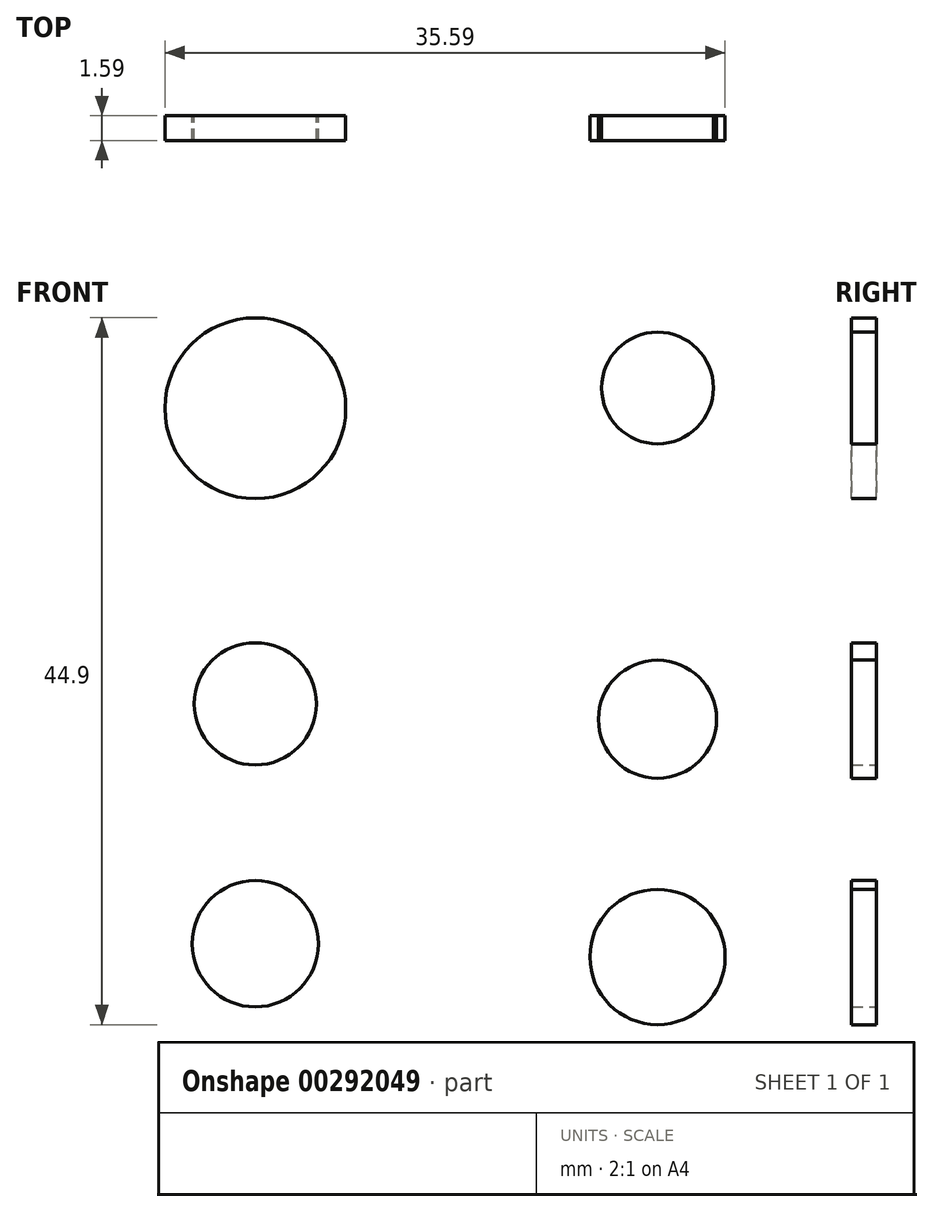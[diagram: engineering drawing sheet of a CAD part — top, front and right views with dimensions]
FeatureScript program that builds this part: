
annotation { "Feature Type Name" : "Feature", "Feature Type Description" : "" }
export const myFeature = defineFeature(function(context is Context, id is Id, definition is map)
    precondition{}
    {
        {
            var Q0;
            Q0=qCreatedBy(makeId("Front.planeOp"),FACE);
            var sketch = newSketch(context, id + "F0", { "sketchPlane" : qUnion([Q0])});
            skCircle(sketch, "E0", {"center": v(-15.42, 19.75) * mm, "radius": 5.74 * mm});
            skCircle(sketch, "E1", {"center": v(-15.42, 0.98) * mm, "radius": 3.88 * mm});
            skCircle(sketch, "E2", {"center": v(-15.42, -14.26) * mm, "radius": 4.01 * mm});
            skCircle(sketch, "E3", {"center": v(10.12, 21.04) * mm, "radius": 3.55 * mm});
            skCircle(sketch, "E4", {"center": v(10.12, 0) * mm, "radius": 3.75 * mm});
            skCircle(sketch, "E5", {"center": v(10.12, -15.1) * mm, "radius": 4.3 * mm});
            skSolve(sketch);
        }
        {
            var Q0;
            Q0 = qSketchRegion(id + "F0", true);
            extrude(context, id + "F1", {"entities" : qUnion([Q0]), "depth" : 1.59 * mm});
        }
    });
